# Revit family: Lithium Lifelight Recessed Emergency_Non_Hosted_R15
name_source: partatom
category: Lighting Fixtures
revit_build: Autodesk Revit 2015 (Build: 20140606_1530(x64)
units: mm (PartAtom-declared; Revit-internal decimal feet)

## types (2) — shared parameters
AS2293 = C0=D32, C90=D32
Apparent Load = 3 W
Battery = P/N: 1530010, L10 3.3V 2.5Ah
Ceiling Hole Cut-Out Radius = 43 mm
Charging Method = Intelligent Current Limited Constant Voltage
Color Filter = 16777215
Colour = Plastic - Polycarbonate - White
Default Elevation = 1219 mm
Description = Lifelight, High Performance, Recessed emergency light
Dimming Lamp Color Temperature Shift = <None>
Height = 42 mm  [stored 0.137795 ft]
Inverter Board = LLIFE-CKIT
Lamp = 1 x 3W LED (Lifetime warranty on the lamp head and loom assembly)
Length = 232 mm  [stored 0.761155 ft]
Manufacturer = Clevertronics
Model = ZLIFE
Mounting = Recessed Ceiling
Operating Mode = Non-Maintained
Operating Voltage = 240 V
Photometric Web File = Lifelight Recessed Emergency.ies
Power Consumption = 3 W
Tilt Angle = 90.00°
Width = 51 mm

## per-type parameters (varying)
| type | Ballast | Testing System | Zoneworks Node |
| LLIFE |  | Manual Test Switch |  |
| LLIFE-ZW | Electronic | Zoneworks Computerised Testing System | P/N: 8001450, Zoneworks Powerline Node |

note: [stored X ft] marks values corroborated as IEEE doubles in the binary element streams (Revit-internal decimal feet)

## geometry (parser evidence)
native form markers: Sweep x3
no freeform markers — native parametric forms only
